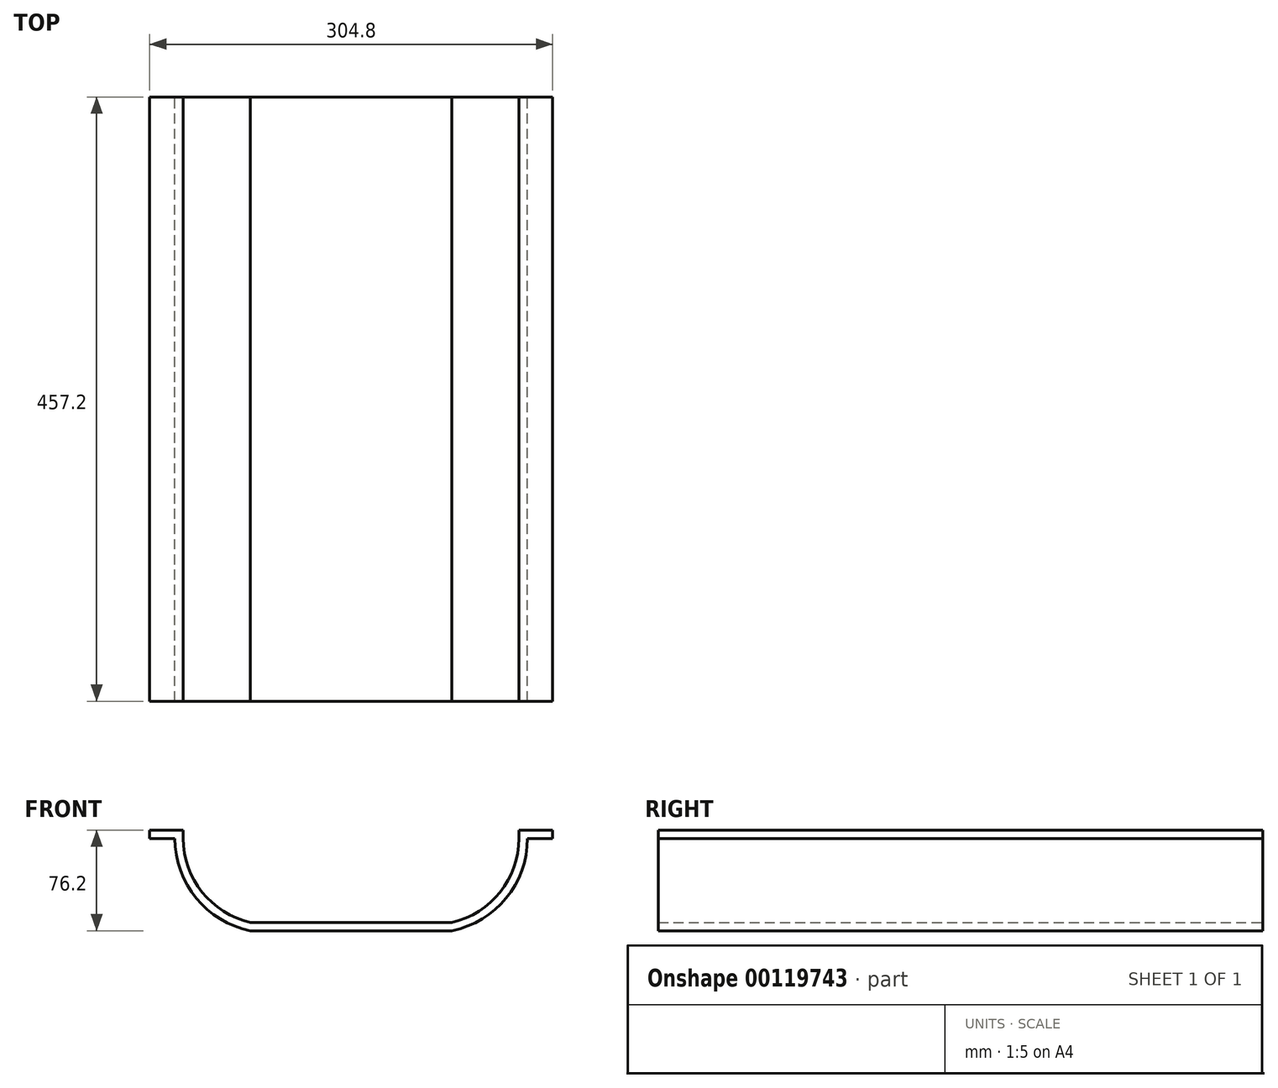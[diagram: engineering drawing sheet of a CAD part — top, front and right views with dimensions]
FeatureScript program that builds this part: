
annotation { "Feature Type Name" : "Feature", "Feature Type Description" : "" }
export const myFeature = defineFeature(function(context is Context, id is Id, definition is map)
    precondition{}
    {
        {
            var Q0;
            Q0=qCreatedBy(makeId("Front.planeOp"),FACE);
            var sketch = newSketch(context, id + "F0", { "sketchPlane" : qUnion([Q0])});
            skLineSegment(sketch, "E0.bottom", {"start": v(-97.4, 0) * mm, "end": v(-72, 0) * mm});
            skLineSegment(sketch, "E0.left", {"start": v(-97.4, 0) * mm, "end": v(-97.4, -6.35) * mm});
            skLineSegment(sketch, "E0.right", {"start": v(169.3, -69.85) * mm, "end": v(169.3, -76.2) * mm});
            skLineSegment(sketch, "E1", {"start": v(-97.4, -6.35) * mm, "end": v(-78.36, -6.35) * mm});
            skPoint(sketch, "E2.orphan", {"position": v(-72, 0) * mm});
            skArc(sketch, "E3", {"start": v(-78.36, -6.35) * mm, "mid": v(-62.25, -51.48) * mm, "end": v(-21.2, -76.2) * mm});
            skArc(sketch, "E4", {"start": v(-72, -6.35) * mm, "mid": v(-57.75, -47) * mm, "end": v(-21.2, -69.85) * mm});
            skLineSegment(sketch, "E5.trimOffspring", {"start": v(-21.2, -76.2) * mm, "end": v(131.2, -76.2) * mm});
            skLineSegment(sketch, "E6.trimOffspring", {"start": v(-21.2, -69.85) * mm, "end": v(131.2, -69.85) * mm});
            skArc(sketch, "E7.MirrorCS", {"start": v(182, -6.35) * mm, "mid": v(167.73, -47) * mm, "end": v(131.2, -69.85) * mm});
            skArc(sketch, "E8.MirrorCS", {"start": v(188.34, -6.35) * mm, "mid": v(172.23, -51.48) * mm, "end": v(131.2, -76.2) * mm});
            skLineSegment(sketch, "E9.MirrorCS", {"start": v(207.4, -6.35) * mm, "end": v(188.34, -6.35) * mm});
            skLineSegment(sketch, "E10.MirrorCS", {"start": v(207.4, 0) * mm, "end": v(182, 0) * mm});
            skLineSegment(sketch, "E11.MirrorCS", {"start": v(207.4, 0) * mm, "end": v(207.4, -6.35) * mm});
            skPoint(sketch, "E12.orphan", {"position": v(169.3, -69.85) * mm});
            skPoint(sketch, "E13.orphan", {"position": v(131.2, -76.2) * mm});
            skPoint(sketch, "E14.start.orphan", {"position": v(-21.2, 0) * mm});
            skPoint(sketch, "E15.start.orphan", {"position": v(55, 0) * mm});
            skLineSegment(sketch, "E16", {"start": v(-72, 0) * mm, "end": v(-72, -6.35) * mm});
            skLineSegment(sketch, "E17", {"start": v(182, -6.35) * mm, "end": v(182, 0) * mm});
            skLineSegment(sketch, "E18", {"start": v(55, -69.85) * mm, "end": v(55, 90.58) * mm});
            skLineSegment(sketch, "E19", {"start": v(-72, 0) * mm, "end": v(182, 0) * mm});
            skSolve(sketch);
        }
        {
            var Q0;
            Q0=makeQuery(id+"F0.imprint","IMPRINT",FACE,{"disambiguationData":[TD([[makeQuery(id+"F0.imprint","IMPRINT",EDGE,{"derivedFrom":sQuery(id+"F0.wireOp",EDGE,"E0.bottom")}),-1.0]])]});
            extrude(context, id + "F1", {"entities" : qUnion([Q0]), "depth" : 457.2 * mm});
        }
    });
